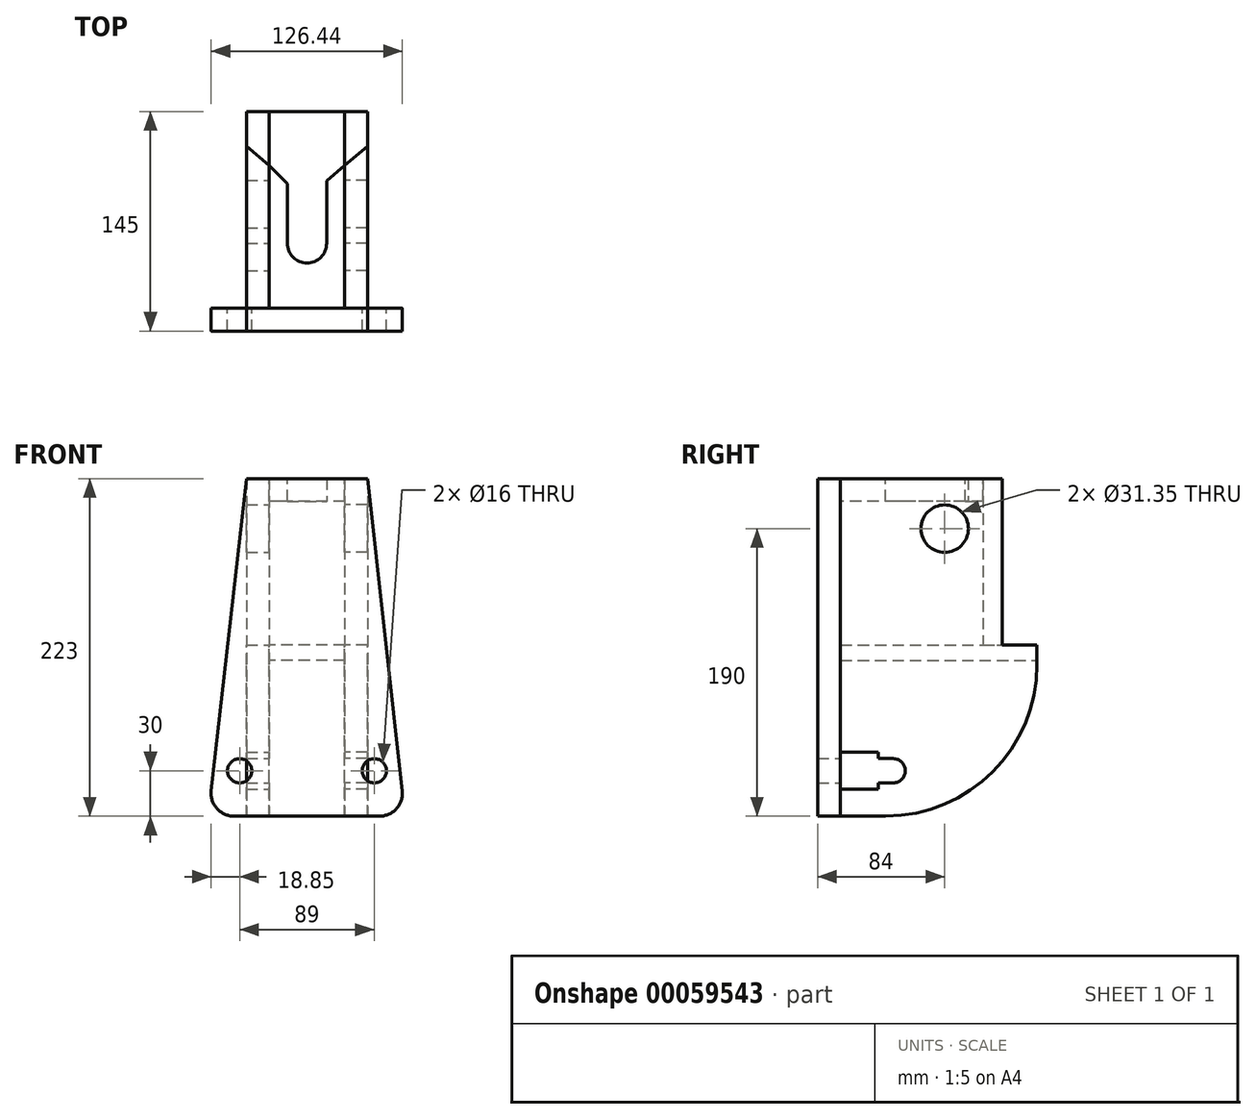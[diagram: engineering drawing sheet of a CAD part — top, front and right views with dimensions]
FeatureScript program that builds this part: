
annotation { "Feature Type Name" : "Feature", "Feature Type Description" : "" }
export const myFeature = defineFeature(function(context is Context, id is Id, definition is map)
    precondition{}
    {
        {
            var Q0;
            Q0=qCreatedBy(makeId("Front.planeOp"),FACE);
            var sketch = newSketch(context, id + "F0", { "sketchPlane" : qUnion([Q0])});
            skLineSegment(sketch, "E0", {"start": v(0, 0) * mm, "end": v(0, -223) * mm, "construction": true});
            skLineSegment(sketch, "E1", {"start": v(0, -223) * mm, "end": v(48.1, -223) * mm});
            skLineSegment(sketch, "E2", {"start": v(0, -223) * mm, "end": v(-48.35, -223) * mm});
            skLineSegment(sketch, "E3", {"start": v(0, 0) * mm, "end": v(40, 0) * mm});
            skLineSegment(sketch, "E4", {"start": v(0, 0) * mm, "end": v(-40, 0) * mm});
            skLineSegment(sketch, "E5", {"start": v(-40, 0) * mm, "end": v(-63.26, -206.32) * mm});
            skLineSegment(sketch, "E6", {"start": v(40, 0) * mm, "end": v(63, -206.34) * mm});
            skLineSegment(sketch, "E7", {"start": v(0, -193) * mm, "end": v(44.5, -193) * mm, "construction": true});
            skLineSegment(sketch, "E8", {"start": v(0, -193) * mm, "end": v(-44.5, -193) * mm, "construction": true});
            skCircle(sketch, "E9", {"center": v(44.5, -193) * mm, "radius": 8 * mm});
            skCircle(sketch, "E10", {"center": v(-44.5, -193) * mm, "radius": 8 * mm});
            skPoint(sketch, "E11.visualSharp", {"position": v(-40, 0) * mm});
            skPoint(sketch, "E12.visualSharp", {"position": v(40, 0) * mm});
            skPoint(sketch, "E13.visualSharp", {"position": v(-65.14, -223) * mm});
            skArc(sketch, "E13.filletArc", {"start": v(-63.26, -206.32) * mm, "mid": v(-59.54, -218) * mm, "end": v(-48.35, -223) * mm});
            skPoint(sketch, "E14.visualSharp", {"position": v(64.86, -223) * mm});
            skArc(sketch, "E14.filletArc", {"start": v(48.1, -223) * mm, "mid": v(59.27, -218) * mm, "end": v(63, -206.34) * mm});
            skSolve(sketch);
        }
        {
            var Q0;
            Q0=makeQuery(id+"F0.imprint","IMPRINT",FACE,{"disambiguationData":[TD([[makeQuery(id+"F0.imprint","IMPRINT",EDGE,{"derivedFrom":sQuery(id+"F0.wireOp",EDGE,"E1")}),1.0]])]});
            extrude(context, id + "F1", {"entities" : qUnion([Q0]), "depth" : 15 * mm});
        }
        {
            var Q0;
            Q0=qCreatedBy(makeId("Right.planeOp"),FACE);
            var sketch = newSketch(context, id + "F2", { "sketchPlane" : qUnion([Q0])});
            skLineSegment(sketch, "E15", {"start": v(0, 0) * mm, "end": v(0, -223) * mm});
            skLineSegment(sketch, "E16", {"start": v(0, 0) * mm, "end": v(107, 0) * mm});
            skLineSegment(sketch, "E17", {"start": v(107, 0) * mm, "end": v(107, -110) * mm});
            skLineSegment(sketch, "E18", {"start": v(107, -110) * mm, "end": v(130, -110) * mm});
            skLineSegment(sketch, "E19", {"start": v(130, -123) * mm, "end": v(130, -110) * mm});
            skLineSegment(sketch, "E20", {"start": v(0, -223) * mm, "end": v(30, -223) * mm});
            skArc(sketch, "E21.filletArc", {"start": v(30, -223) * mm, "mid": v(100.71, -193.71) * mm, "end": v(130, -123) * mm});
            skCircle(sketch, "E22", {"center": v(69, -33) * mm, "radius": 15.68 * mm});
            skLineSegment(sketch, "E23", {"start": v(25, -180.75) * mm, "end": v(0, -180.75) * mm});
            skLineSegment(sketch, "E24", {"start": v(25, -205.25) * mm, "end": v(0, -205.25) * mm});
            skLineSegment(sketch, "E25", {"start": v(43, -193) * mm, "end": v(0, -193) * mm, "construction": true});
            skPoint(sketch, "E25.endSnap0", {"position": v(35, -193) * mm});
            skLineSegment(sketch, "E26", {"start": v(35, -185) * mm, "end": v(25, -185) * mm});
            skLineSegment(sketch, "E27.MirrorCS", {"start": v(35, -201) * mm, "end": v(25, -201) * mm});
            skArc(sketch, "E28", {"start": v(35, -201) * mm, "mid": v(43, -193) * mm, "end": v(35, -185) * mm});
            skLineSegment(sketch, "E29", {"start": v(25, -180.75) * mm, "end": v(25, -185) * mm});
            skLineSegment(sketch, "E30", {"start": v(25, -201) * mm, "end": v(25, -205.25) * mm});
            skSolve(sketch);
        }
        {
            var Q0;
            {var subQ1=sQuery(id+"F2.wireOp",EDGE,"E16");Q0=makeQuery(id+"F2.imprint","IMPRINT",FACE,{"disambiguationData":[TD([[makeQuery(id+"F2.imprint","IMPRINT",EDGE,{"derivedFrom":subQ1}),-1.0]])]});}
            extrude(context, id + "F3", {"entities" : qUnion([Q0]), "depth" : 40 * mm, "hasSecondDirection" : true, "secondDirectionOppositeDirection" : false, "secondDirectionDepth" : 25 * mm});
        }
        {
            var Q0;
            Q0=makeQuery(id+"F3.opExtrude","CAP_EDGE",EDGE,{"disambiguationData":[OSD([sQuery(id+"F2.wireOp",EDGE,"E17")])],"isStart":true});
            chamfer(context, id + "F4", {"entities" : qUnion([Q0]), "chamferType" : ChamferType.OFFSET_ANGLE, "width" : 15 * mm, "oppositeDirection" : true, "angle" : 40 * degree, "tangentPropagation" : true});
        }
        {
            var Q0;
            Q0=makeQuery(id+"F3.opExtrude","SWEPT_BODY",BODY,{"disambiguationData":[OSD([sQuery(id+"F2.wireOp",EDGE,"E15"),sQuery(id+"F2.wireOp",EDGE,"E16"),sQuery(id+"F2.wireOp",EDGE,"E17"),sQuery(id+"F2.wireOp",EDGE,"E18"),sQuery(id+"F2.wireOp",EDGE,"E19"),sQuery(id+"F2.wireOp",EDGE,"E20"),sQuery(id+"F2.wireOp",EDGE,"E21.filletArc")])]});
            var Q1;
            Q1=qCreatedBy(makeId("Right.planeOp"),FACE);
            mirror(context, id + "F5", {"entities" : qUnion([Q0]), "mirrorPlane" : qUnion([Q1])});
        }
        {
            var Q0;
            Q0=qCreatedBy(makeId("Top.planeOp"),FACE);
            var sketch = newSketch(context, id + "F6", { "sketchPlane" : qUnion([Q0])});
            skLineSegment(sketch, "E31", {"start": v(0, 0) * mm, "end": v(25, 0) * mm});
            skLineSegment(sketch, "E32", {"start": v(0, 0) * mm, "end": v(-25, 0) * mm});
            skLineSegment(sketch, "E33", {"start": v(-25, 0) * mm, "end": v(-25, 94.41) * mm});
            skLineSegment(sketch, "E34", {"start": v(-25, 94.41) * mm, "end": v(25, 94.41) * mm, "construction": true});
            skLineSegment(sketch, "E35", {"start": v(25, 94.41) * mm, "end": v(25, 0) * mm});
            skLineSegment(sketch, "E36", {"start": v(-25, 94.41) * mm, "end": v(-13, 94.41) * mm});
            skLineSegment(sketch, "E37", {"start": v(-13, 94.41) * mm, "end": v(-13, 43) * mm});
            skLineSegment(sketch, "E38.MirrorCS", {"start": v(25, 94.41) * mm, "end": v(13, 94.41) * mm});
            skLineSegment(sketch, "E39.MirrorCS", {"start": v(13, 94.41) * mm, "end": v(13, 43) * mm});
            skLineSegment(sketch, "E40", {"start": v(0, 30) * mm, "end": v(0, 30) * mm});
            skArc(sketch, "E41.filletArc", {"start": v(-13, 43) * mm, "mid": v(-9.2, 33.8) * mm, "end": v(0, 30) * mm});
            skArc(sketch, "E42.filletArc", {"start": v(0, 30) * mm, "mid": v(9.2, 33.8) * mm, "end": v(13, 43) * mm});
            skSolve(sketch);
        }
        {
            var Q0;
            Q0=makeQuery(id+"F6.imprint","IMPRINT",FACE,{"disambiguationData":[TD([[makeQuery(id+"F6.imprint","IMPRINT",EDGE,{"derivedFrom":sQuery(id+"F6.wireOp",EDGE,"E31")}),1.0]])]});
            extrude(context, id + "F7", {"entities" : qUnion([Q0]), "oppositeDirection" : true, "depth" : 15 * mm});
        }
        {
            var Q0;
            Q0=makeQuery(id+"F7.opExtrude","SWEPT_EDGE",EDGE,{"disambiguationData":[OSD([sQuery(id+"F6.wireOp",EDGE,"E38.MirrorCS"),sQuery(id+"F6.wireOp",EDGE,"E39.MirrorCS")])]});
            chamfer(context, id + "F8", {"entities" : qUnion([Q0]), "chamferType" : ChamferType.OFFSET_ANGLE, "width" : 12 * mm, "oppositeDirection" : false, "angle" : 40 * degree, "tangentPropagation" : true});
        }
        {
            var Q0;
            Q0=makeQuery(id+"F7.opExtrude","SWEPT_EDGE",EDGE,{"disambiguationData":[OSD([sQuery(id+"F6.wireOp",EDGE,"E36"),sQuery(id+"F6.wireOp",EDGE,"E37")])]});
            chamfer(context, id + "F9", {"entities" : qUnion([Q0]), "chamferType" : ChamferType.OFFSET_ANGLE, "width" : 12 * mm, "oppositeDirection" : false, "angle" : 45 * degree, "tangentPropagation" : true});
        }
        {
            var Q0;
            Q0=qCreatedBy(makeId("Top.planeOp"),FACE);
            var sketch = newSketch(context, id + "F10", { "sketchPlane" : qUnion([Q0])});
            skLineSegment(sketch, "E43", {"start": v(0, 0) * mm, "end": v(-25, 0) * mm});
            skLineSegment(sketch, "E44", {"start": v(-25, 0) * mm, "end": v(-25, 130) * mm});
            skLineSegment(sketch, "E45", {"start": v(-25, 130) * mm, "end": v(25, 130) * mm});
            skLineSegment(sketch, "E46", {"start": v(0, 0) * mm, "end": v(25, 0) * mm});
            skLineSegment(sketch, "E47", {"start": v(25, 0) * mm, "end": v(25, 130) * mm});
            skSolve(sketch);
        }
        {
            var Q0;
            Q0=makeQuery(id+"F10.imprint","IMPRINT",FACE,{"disambiguationData":[TD([[makeQuery(id+"F10.imprint","IMPRINT",EDGE,{"derivedFrom":sQuery(id+"F10.wireOp",EDGE,"E43")}),-1.0]])]});
            extrude(context, id + "F11", {"entities" : qUnion([Q0]), "oppositeDirection" : true, "depth" : 120 * mm, "hasSecondDirection" : true, "secondDirectionOppositeDirection" : true, "secondDirectionDepth" : 110 * mm});
        }
    });
